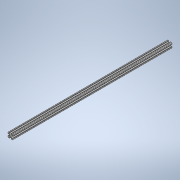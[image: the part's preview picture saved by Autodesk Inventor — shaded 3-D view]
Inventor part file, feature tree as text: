
AUTODESK INVENTOR PART (.ipt)
format: ipt  version: 2020 (Build 240168000, 168)  size: 242,688 bytes
history: native  units: in
note: dims shown in document units (in); Inventor stores cm internally (conversion verified against a paired STEP export)
features: extrude x1, sketch x1
ambient origin geometry x8: Origin, YZ Plane, XZ Plane, XY Plane, X Axis, Y Axis, Z Axis, Center Point
bodies: Solid1 (feature_tree)
feature tree (2):
  extrude  "Extrusion1"  [1 undecoded]
  sketch  "Sketch1"  dims[d0=32.0in d1=0.0in]
note: 1 required parameter value undecoded (feature->parameter linkage not recoverable at this tier; creation-order binding heuristic only, values carry confidence <= 0.55)
